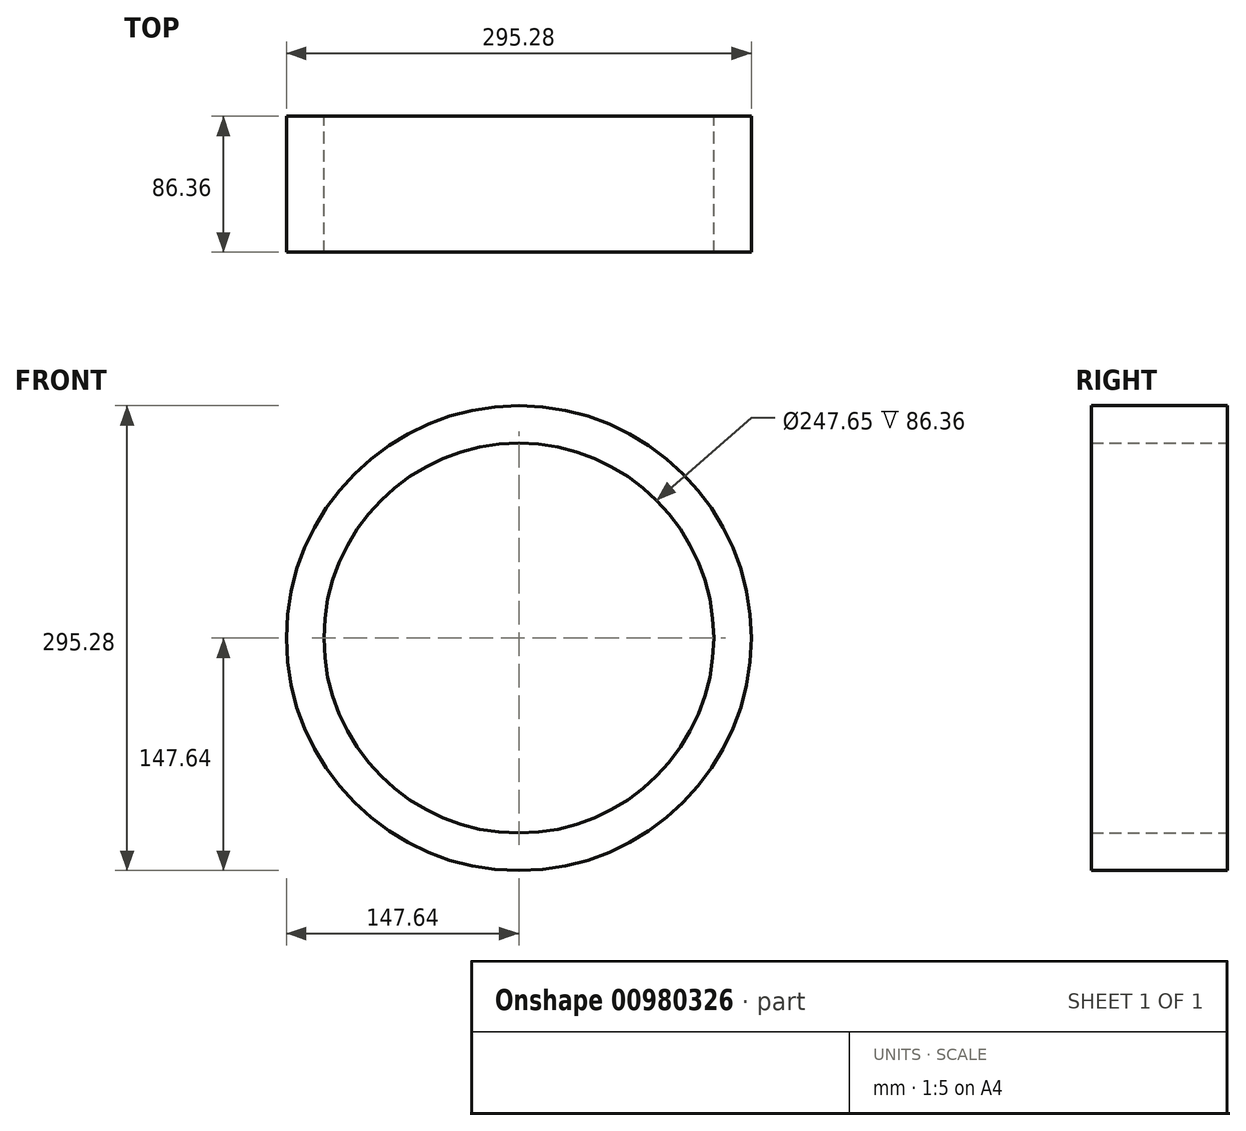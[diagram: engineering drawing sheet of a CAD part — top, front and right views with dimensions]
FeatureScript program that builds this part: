
annotation { "Feature Type Name" : "Feature", "Feature Type Description" : "" }
export const myFeature = defineFeature(function(context is Context, id is Id, definition is map)
    precondition{}
    {
        {
            var Q0;
            Q0=qCreatedBy(makeId("Front.planeOp"),FACE);
            var sketch = newSketch(context, id + "F0", { "sketchPlane" : qUnion([Q0])});
            skCircle(sketch, "E0", {"center": v(0, 0) * mm, "radius": 123.83 * mm});
            skCircle(sketch, "E1", {"center": v(0, 0) * mm, "radius": 147.64 * mm});
            skSolve(sketch);
        }
        {
            var Q0;
            Q0 = qSketchRegion(id + "F0", true);
            extrude(context, id + "F1", {"entities" : qUnion([Q0]), "endBound" : BoundingType.SYMMETRIC, "depth" : 86.36 * mm, "offsetDistance" : 25.4 * mm});
        }
    });
